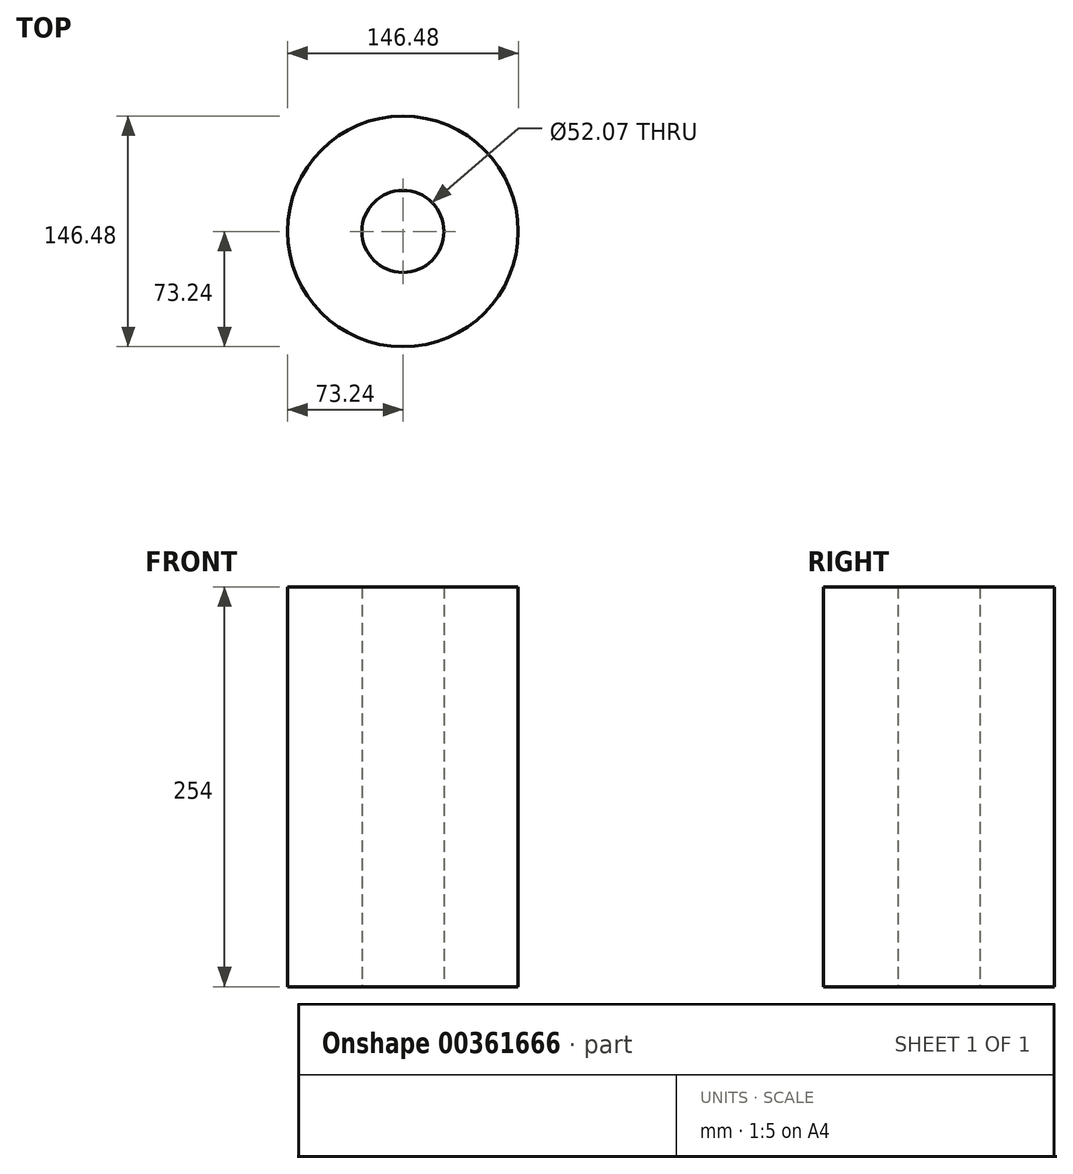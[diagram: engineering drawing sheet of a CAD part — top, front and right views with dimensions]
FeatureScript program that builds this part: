
annotation { "Feature Type Name" : "Feature", "Feature Type Description" : "" }
export const myFeature = defineFeature(function(context is Context, id is Id, definition is map)
    precondition{}
    {
        {
            var Q0;
            Q0=qCreatedBy(makeId("Top.planeOp"),FACE);
            var sketch = newSketch(context, id + "F0", { "sketchPlane" : qUnion([Q0])});
            skCircle(sketch, "E0", {"center": v(0, 0) * mm, "radius": 73.24 * mm});
            skCircle(sketch, "E1", {"center": v(0, 0) * mm, "radius": 26.04 * mm});
            skSolve(sketch);
        }
        {
            var Q0;
            Q0=makeQuery(id+"F0.imprint","IMPRINT",FACE,{"disambiguationData":[TD([[makeQuery(id+"F0.imprint","IMPRINT",EDGE,{"derivedFrom":sQuery(id+"F0.wireOp",EDGE,"E0")}),1.0]])]});
            extrude(context, id + "F1", {"entities" : qUnion([Q0]), "depth" : 254 * mm});
        }
    });
